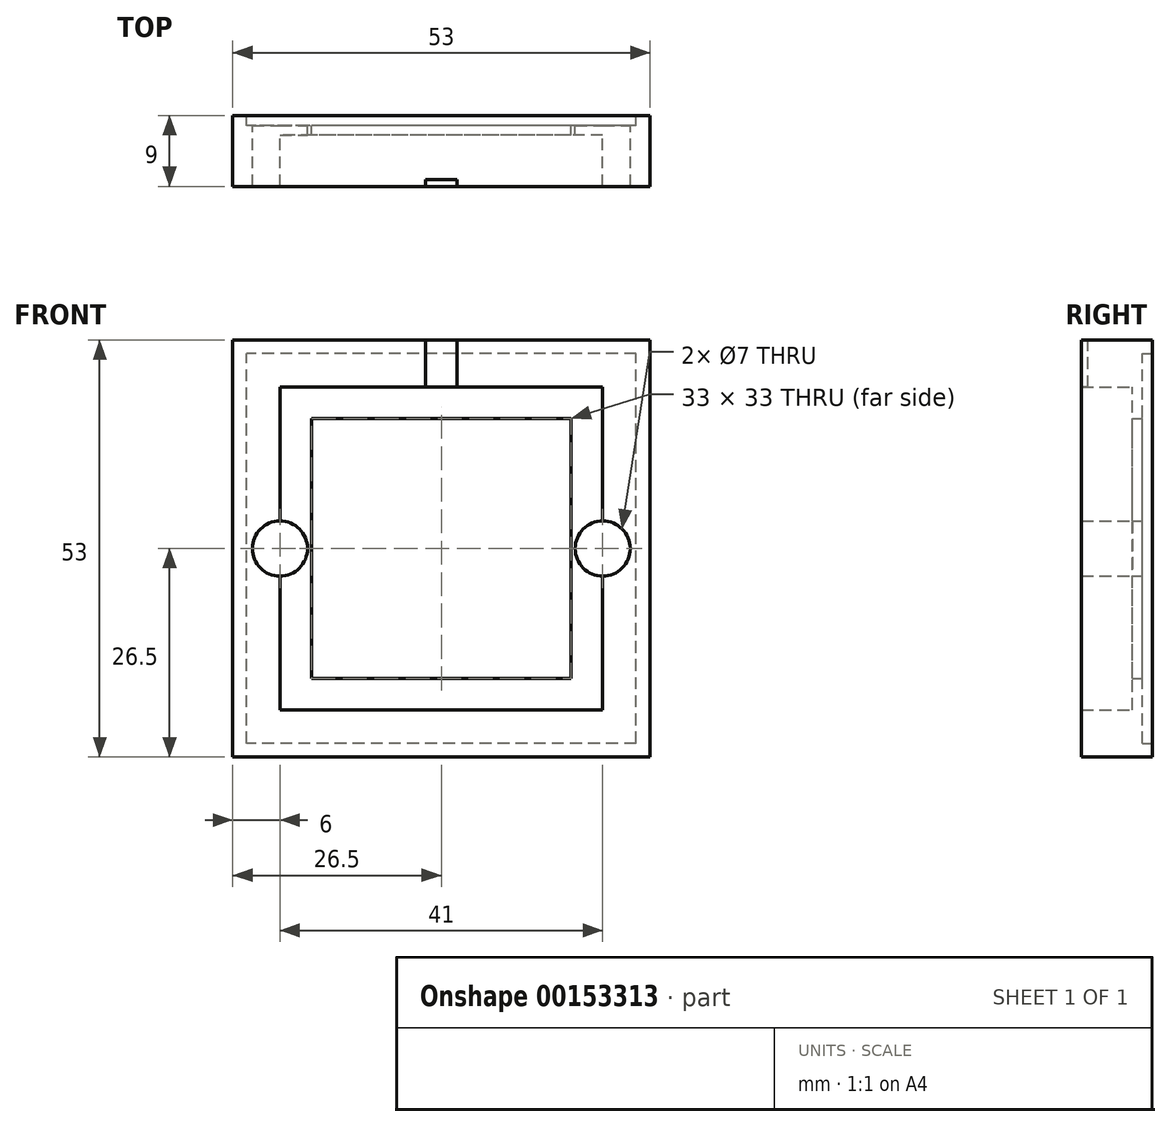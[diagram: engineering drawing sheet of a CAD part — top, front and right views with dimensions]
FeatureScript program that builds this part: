
annotation { "Feature Type Name" : "Feature", "Feature Type Description" : "" }
export const myFeature = defineFeature(function(context is Context, id is Id, definition is map)
    precondition{}
    {
        {
            var Q0;
            Q0=qCreatedBy(makeId("Front.planeOp"),FACE);
            var sketch = newSketch(context, id + "F0", { "sketchPlane" : qUnion([Q0])});
            skLineSegment(sketch, "E0.bottom", {"start": v(16.5, -16.5) * mm, "end": v(-16.5, -16.5) * mm});
            skLineSegment(sketch, "E0.top", {"start": v(16.5, 16.5) * mm, "end": v(-16.5, 16.5) * mm});
            skLineSegment(sketch, "E0.left", {"start": v(16.5, -16.5) * mm, "end": v(16.5, 16.5) * mm});
            skLineSegment(sketch, "E0.right", {"start": v(-16.5, -16.5) * mm, "end": v(-16.5, 16.5) * mm});
            skPoint(sketch, "E0.middle", {"position": v(0, 0) * mm});
            skLineSegment(sketch, "E1.0", {"start": v(-26.5, -26.5) * mm, "end": v(-26.5, 26.5) * mm});
            skLineSegment(sketch, "E1.1", {"start": v(26.5, -26.5) * mm, "end": v(-26.5, -26.5) * mm});
            skLineSegment(sketch, "E1.2", {"start": v(26.5, -26.5) * mm, "end": v(26.5, 26.5) * mm});
            skLineSegment(sketch, "E1.3", {"start": v(26.5, 26.5) * mm, "end": v(-26.5, 26.5) * mm});
            skLineSegment(sketch, "E2.0", {"start": v(-24.75, -24.75) * mm, "end": v(-24.75, 24.75) * mm});
            skLineSegment(sketch, "E2.1", {"start": v(24.75, -24.75) * mm, "end": v(-24.75, -24.75) * mm});
            skLineSegment(sketch, "E2.2", {"start": v(24.75, -24.75) * mm, "end": v(24.75, 24.75) * mm});
            skLineSegment(sketch, "E2.3", {"start": v(24.75, 24.75) * mm, "end": v(-24.75, 24.75) * mm});
            skLineSegment(sketch, "E3.0", {"start": v(20.5, -20.5) * mm, "end": v(20.5, 20.5) * mm});
            skLineSegment(sketch, "E3.1", {"start": v(20.5, -20.5) * mm, "end": v(-20.5, -20.5) * mm});
            skLineSegment(sketch, "E3.2", {"start": v(-20.5, -20.5) * mm, "end": v(-20.5, 20.5) * mm});
            skLineSegment(sketch, "E3.3", {"start": v(20.5, 20.5) * mm, "end": v(-20.5, 20.5) * mm});
            skPoint(sketch, "E4", {"position": v(20.5, 0) * mm});
            skPoint(sketch, "E5", {"position": v(-20.5, 0) * mm});
            skCircle(sketch, "E6", {"center": v(20.5, 0) * mm, "radius": 1.88 * mm});
            skCircle(sketch, "E7", {"center": v(-20.5, 0) * mm, "radius": 1.88 * mm});
            skCircle(sketch, "E8", {"center": v(20.5, 0) * mm, "radius": 3.5 * mm});
            skCircle(sketch, "E9", {"center": v(-20.5, 0) * mm, "radius": 3.5 * mm});
            skSolve(sketch);
        }
        {
            var Q0;
            Q0=makeQuery(id+"F0.imprint","IMPRINT",FACE,{"disambiguationData":[TD([[makeQuery(id+"F0.imprint","IMPRINT",EDGE,{"derivedFrom":sQuery(id+"F0.wireOp",EDGE,"E0.bottom")}),1.0]])]});
            extrude(context, id + "F1", {"entities" : qUnion([Q0]), "depth" : 2.5 * mm});
        }
        {
            var Q0;
            Q0=makeQuery(id+"F0.imprint","IMPRINT",FACE,{"disambiguationData":[TD([[makeQuery(id+"F0.imprint","IMPRINT",EDGE,{"derivedFrom":sQuery(id+"F0.wireOp",EDGE,"E1.0")}),-1.0]])]});
            var Q1;
            Q1=makeQuery(id+"F0.imprint","IMPRINT",FACE,{"disambiguationData":[TD([[makeQuery(id+"F0.imprint","IMPRINT",EDGE,{"derivedFrom":sQuery(id+"F0.wireOp",EDGE,"E2.0")}),-1.0]])]});
            extrude(context, id + "F2", {"entities" : qUnion([Q0, Q1]), "operationType" : NewBodyOperationType.ADD, "depth" : 9 * mm});
        }
        {
            var Q0;
            Q0=makeQuery(id+"F2.opExtrude","SWEPT_FACE",FACE,{"disambiguationData":[OSD([sQuery(id+"F0.wireOp",EDGE,"E1.3")])]});
            var sketch = newSketch(context, id + "F3", { "sketchPlane" : qUnion([Q0])});
            skLineSegment(sketch, "E10.bottom", {"start": v(2, -9.85) * mm, "end": v(-2, -9.85) * mm});
            skLineSegment(sketch, "E10.top", {"start": v(2, -8.15) * mm, "end": v(-2, -8.15) * mm});
            skLineSegment(sketch, "E10.left", {"start": v(2, -9.85) * mm, "end": v(2, -8.15) * mm});
            skLineSegment(sketch, "E10.right", {"start": v(-2, -9.85) * mm, "end": v(-2, -8.15) * mm});
            skPoint(sketch, "E10.middle", {"position": v(0, -9) * mm});
            skSolve(sketch);
        }
        {
            var Q0;
            {var subQ0=sQuery(id+"F3.wireOp",EDGE,"E10.top");Q0=makeQuery(id+"F3.imprint","IMPRINT",FACE,{"disambiguationData":[TD([[makeQuery(id+"F3.imprint","IMPRINT",EDGE,{"derivedFrom":subQ0}),1.0]])]});}
            extrude(context, id + "F4", {"entities" : qUnion([Q0]), "operationType" : NewBodyOperationType.REMOVE, "oppositeDirection" : true, "depth" : 6.75 * mm});
        }
        {
            var Q0;
            {var subQ0=sQuery(id+"F0.wireOp",EDGE,"E8");var subQ1=sQuery(id+"F0.wireOp",EDGE,"E3.0");var subQ2=makeQuery(id+"F0.imprint","INTERSECT",VERTEX,{"disambiguationData":[OD(0.0)],"derivedFrom":[subQ1,subQ0]});Q0=makeQuery(id+"F0.imprint","IMPRINT",FACE,{"disambiguationData":[TD([[makeQuery(id+"F0.imprint","IMPRINT",EDGE,{"disambiguationData":[TD([[subQ2,-1.0]])],"derivedFrom":subQ1}),1.0]])]});}
            var Q1;
            {var subQ0=sQuery(id+"F0.wireOp",EDGE,"E8");var subQ1=sQuery(id+"F0.wireOp",EDGE,"E3.0");var subQ2=makeQuery(id+"F0.imprint","INTERSECT",VERTEX,{"disambiguationData":[OD(0.0)],"derivedFrom":[subQ1,subQ0]});Q1=makeQuery(id+"F0.imprint","IMPRINT",FACE,{"disambiguationData":[TD([[makeQuery(id+"F0.imprint","IMPRINT",EDGE,{"disambiguationData":[TD([[subQ2,-1.0]])],"derivedFrom":subQ1}),-1.0]])]});}
            var Q2;
            {var subQ0=sQuery(id+"F0.wireOp",EDGE,"E9");var subQ1=sQuery(id+"F0.wireOp",EDGE,"E3.2");var subQ2=makeQuery(id+"F0.imprint","INTERSECT",VERTEX,{"disambiguationData":[OD(0.0)],"derivedFrom":[subQ1,subQ0]});Q2=makeQuery(id+"F0.imprint","IMPRINT",FACE,{"disambiguationData":[TD([[makeQuery(id+"F0.imprint","IMPRINT",EDGE,{"disambiguationData":[TD([[subQ2,-1.0]])],"derivedFrom":subQ1}),-1.0]])]});}
            var Q3;
            {var subQ0=sQuery(id+"F0.wireOp",EDGE,"E9");var subQ1=sQuery(id+"F0.wireOp",EDGE,"E3.2");var subQ2=makeQuery(id+"F0.imprint","INTERSECT",VERTEX,{"disambiguationData":[OD(0.0)],"derivedFrom":[subQ1,subQ0]});Q3=makeQuery(id+"F0.imprint","IMPRINT",FACE,{"disambiguationData":[TD([[makeQuery(id+"F0.imprint","IMPRINT",EDGE,{"disambiguationData":[TD([[subQ2,-1.0]])],"derivedFrom":subQ1}),1.0]])]});}
            extrude(context, id + "F5", {"entities" : qUnion([Q0, Q1, Q2, Q3]), "operationType" : NewBodyOperationType.ADD, "depth" : 2.5 * mm});
        }
        {
            var Q0;
            {var subQ0=sQuery(id+"F0.wireOp",EDGE,"E8");var subQ1=sQuery(id+"F0.wireOp",EDGE,"E3.0");var subQ2=makeQuery(id+"F0.imprint","INTERSECT",VERTEX,{"disambiguationData":[OD(0.0)],"derivedFrom":[subQ1,subQ0]});Q0=makeQuery(id+"F0.imprint","IMPRINT",FACE,{"disambiguationData":[TD([[makeQuery(id+"F0.imprint","IMPRINT",EDGE,{"disambiguationData":[TD([[subQ2,-1.0]])],"derivedFrom":subQ1}),1.0]])]});}
            var Q1;
            {var subQ0=sQuery(id+"F0.wireOp",EDGE,"E8");var subQ1=sQuery(id+"F0.wireOp",EDGE,"E3.0");var subQ2=makeQuery(id+"F0.imprint","INTERSECT",VERTEX,{"disambiguationData":[OD(0.0)],"derivedFrom":[subQ1,subQ0]});Q1=makeQuery(id+"F0.imprint","IMPRINT",FACE,{"disambiguationData":[TD([[makeQuery(id+"F0.imprint","IMPRINT",EDGE,{"disambiguationData":[TD([[subQ2,-1.0]])],"derivedFrom":subQ1}),-1.0]])]});}
            var Q2;
            {var subQ0=sQuery(id+"F0.wireOp",EDGE,"E9");var subQ1=sQuery(id+"F0.wireOp",EDGE,"E3.2");var subQ2=makeQuery(id+"F0.imprint","INTERSECT",VERTEX,{"disambiguationData":[OD(0.0)],"derivedFrom":[subQ1,subQ0]});Q2=makeQuery(id+"F0.imprint","IMPRINT",FACE,{"disambiguationData":[TD([[makeQuery(id+"F0.imprint","IMPRINT",EDGE,{"disambiguationData":[TD([[subQ2,-1.0]])],"derivedFrom":subQ1}),-1.0]])]});}
            var Q3;
            {var subQ0=sQuery(id+"F0.wireOp",EDGE,"E9");var subQ1=sQuery(id+"F0.wireOp",EDGE,"E3.2");var subQ2=makeQuery(id+"F0.imprint","INTERSECT",VERTEX,{"disambiguationData":[OD(0.0)],"derivedFrom":[subQ1,subQ0]});Q3=makeQuery(id+"F0.imprint","IMPRINT",FACE,{"disambiguationData":[TD([[makeQuery(id+"F0.imprint","IMPRINT",EDGE,{"disambiguationData":[TD([[subQ2,-1.0]])],"derivedFrom":subQ1}),1.0]])]});}
            var Q4;
            Q4=sQuery(id+"F0.wireOp",EDGE,"E8");
            var Q5;
            Q5=sQuery(id+"F0.wireOp",EDGE,"E9");
            extrude(context, id + "F6", {"entities" : qUnion([Q0, Q1, Q2, Q3]), "operationType" : NewBodyOperationType.REMOVE, "surfaceEntities" : qUnion([Q4, Q5]), "depth" : 1.25 * mm});
        }
    });
